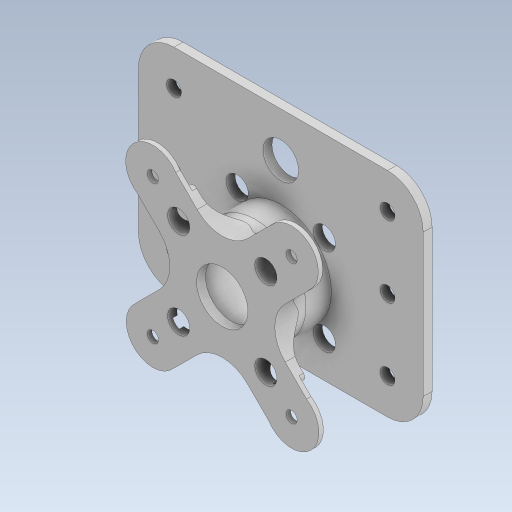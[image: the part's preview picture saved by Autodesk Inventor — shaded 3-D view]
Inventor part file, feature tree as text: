
AUTODESK INVENTOR PART (.ipt)
format: ipt  version: 2023 (Build 270158000, 158)  size: 439,296 bytes
history: native  units: in
note: dims shown in document units (in); Inventor stores cm internally (conversion verified against a paired STEP export)
features: reference x9, extrude x5, sketch x5, other x4, plane x2, fillet x2, projected_geometry x2
ambient origin geometry x8: Origin, YZ Plane, XZ Plane, XY Plane, X Axis, Y Axis, Z Axis, Center Point
bodies: Solid1 (feature_tree)
feature tree (29):
  plane  "Work Plane1"
  extrude  "Extrusion1"  Depth=0.5in
  plane  "Work Plane2"
  extrude  "Extrusion2"  Depth=0.3125in
  extrude  "Extrusion3"  Depth=0.0625in TaperAngle=0.0deg
  extrude  "Extrusion5"  Depth=0.0625in TaperAngle=0.0deg
  extrude  "Extrusion4"  TaperAngle=0.0deg  [1 undecoded]
  fillet  "Fillet2"  Radius=0.0625in
  fillet  "Fillet3"  Radius=0.34in
  sketch  "Sketch1"  dims[d0=0.5in d1=0.5in]
  reference  "Reference1"
  reference  "Reference2"
  sketch  "Sketch2"  dims[d2=0.125in d3=0.0in d4=0.3125in]
  reference  "Reference3"
  sketch  "Sketch4"  dims[d5=1.5748in d7=360.0deg d9=0.0625in d10=0.0in]
  projected_geometry  "Projected Loop1"
  reference  "Reference4"
  reference  "Reference5"
  reference  "Reference6"
  reference  "Reference7"
  reference  "Reference8"
  sketch  "Sketch5"  dims[d11=0.0625in d12=0.0in d13=0.0625in d14=0.0in]
  reference  "Reference9"
  sketch  "Sketch6"  dims[d15=1.125in d17=0.0in d18=0.0in d19=0.0625in d20=0.34in]
  projected_geometry  "Projected Loop2"
  other  "Gearbox Assembly.iam"
  other  "CH-1-02-RearGearboxHousingMotorSide:1"
  other  "DriveMotorPlate:1"
  other  "Drive Motor Shaft Coupler:1"
note: 1 required parameter value undecoded (feature->parameter linkage not recoverable at this tier; creation-order binding heuristic only, values carry confidence <= 0.55)
